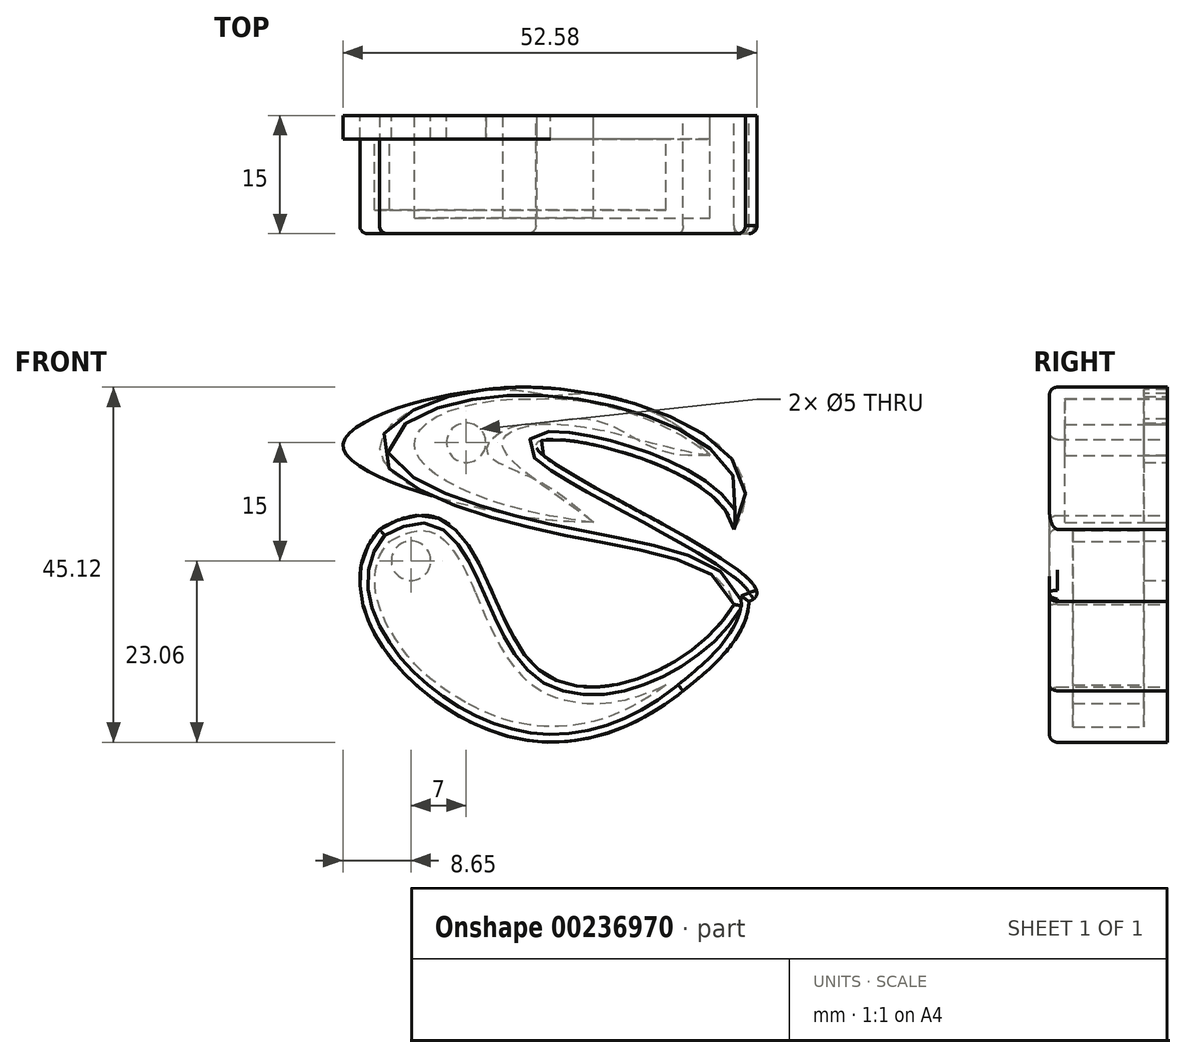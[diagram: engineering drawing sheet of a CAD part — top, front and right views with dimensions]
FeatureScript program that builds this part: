
annotation { "Feature Type Name" : "Feature", "Feature Type Description" : "" }
export const myFeature = defineFeature(function(context is Context, id is Id, definition is map)
    precondition{}
    {
        {
            var Q0;
            Q0=qCreatedBy(makeId("Front.planeOp"),FACE);
            var sketch = newSketch(context, id + "F0", { "sketchPlane" : qUnion([Q0])});
            skLineSegment(sketch, "E0", {"start": v(0, 18.03) * mm, "end": v(0, -26.97) * mm, "construction": true});
            skFitSpline(sketch, "E1", {"points": [v(25, 0) * mm, v(0, 18.03) * mm, v(-20, 10.22) * mm, v(0, 0) * mm, v(25, -9.54) * mm, v(0, -26.97) * mm, v(-20, 0) * mm], "startDerivative": vector(114.8, 173.45) * mm, "endDerivative": vector(137.84, 155.21) * mm});
            skLineSegment(sketch, "E2", {"start": v(-20, 0) * mm, "end": v(25, 0) * mm, "construction": true});
            skFitSpline(sketch, "E3", {"points": [v(25, 0) * mm, v(0, 10.22) * mm, v(25, -9.54) * mm], "startDerivative": vector(-9.3, 54.04) * mm, "endDerivative": vector(-76.27, -7.07) * mm});
            skFitSpline(sketch, "E4", {"points": [v(-20, 0) * mm, v(0, -17.65) * mm, v(25, -9.54) * mm], "startDerivative": vector(77.62, 45.8) * mm, "endDerivative": vector(25.53, 45.41) * mm});
            skFitSpline(sketch, "E5", {"points": [v(25.52, -5.18) * mm, v(17.95, -21.02) * mm], "startDerivative": vector(15.34, -20.4) * mm, "endDerivative": vector(-6.86, -5.89) * mm});
            skSolve(sketch);
        }
        {
            var Q0;
            Q0 = qSketchRegion(id + "F0", true);
            extrude(context, id + "F1", {"entities" : qUnion([Q0]), "depth" : 15 * mm});
        }
        {
            var Q0;
            Q0=makeQuery(id+"F1.opExtrude","CAP_FACE",FACE,{"disambiguationData":[OSD([sQuery(id+"F0.wireOp",EDGE,"E1"),sQuery(id+"F0.wireOp",EDGE,"E3"),sQuery(id+"F0.wireOp",EDGE,"E4"),sQuery(id+"F0.wireOp",EDGE,"E5"),sQuery(id+"F0.wireOp",EDGE,"E1")])],"isStart":true});
            var sketch = newSketch(context, id + "F2", { "sketchPlane" : qUnion([Q0])});
            skFitSpline(sketch, "E6.0", {"points": [v(-25, 0) * mm, v(-31.76, 10.22) * mm, v(1.18, 23.58) * mm, v(29, 9.83) * mm, v(0.24, -1.74) * mm, v(-37.75, -4.5) * mm, v(0.03, -41.05) * mm, v(28.48, -9.54) * mm, v(20, 0) * mm]});
            skFitSpline(sketch, "E7.0", {"points": [v(20, 0) * mm, v(7.02, 7.66) * mm, v(6.98, -30.5) * mm, v(-20.76, -17.08) * mm, v(-25, -9.54) * mm]});
            skFitSpline(sketch, "E8.0", {"points": [v(-25.52, -5.18) * mm, v(-30.63, -11.98) * mm, v(-20.23, -19.06) * mm, v(-17.95, -21.02) * mm]});
            skFitSpline(sketch, "E9.0", {"points": [v(-25, 0) * mm, v(-23.51, 8.63) * mm, v(30.37, 19.61) * mm, v(-38.24, -8.32) * mm, v(-25, -9.54) * mm]});
            skFitSpline(sketch, "E10.0", {"points": [v(-25, 0) * mm, v(-31.76, 10.22) * mm, v(1.18, 23.58) * mm, v(29, 9.83) * mm, v(0.24, -1.74) * mm, v(-37.75, -4.5) * mm, v(0.03, -41.05) * mm, v(28.48, -9.54) * mm, v(20, 0) * mm]});
            skFitSpline(sketch, "E11.0", {"points": [v(18.98, -1.72) * mm, v(18.25, -1.3) * mm, v(16.92, -0.64) * mm, v(15.34, -0.22) * mm, v(14.13, -0.2) * mm, v(13.16, -0.45) * mm, v(12.25, -0.98) * mm, v(11.33, -1.84) * mm, v(10.41, -3.03) * mm, v(9.24, -5) * mm, v(7.84, -8.02) * mm, v(6.43, -11.33) * mm, v(5.17, -13.93) * mm, v(4.11, -15.8) * mm, v(3.1, -17.26) * mm, v(2.18, -18.33) * mm, v(1.43, -19.08) * mm, v(0.6, -19.75) * mm, v(-0.55, -20.52) * mm, v(-2.09, -21.26) * mm, v(-4.04, -21.81) * mm, v(-6.72, -22.14) * mm, v(-10.14, -21.88) * mm, v(-14.2, -20.72) * mm, v(-18.07, -18.88) * mm, v(-21.59, -16.5) * mm, v(-24.6, -13.7) * mm, v(-26.13, -11.62) * mm, v(-26.74, -10.52) * mm]});
            skFitSpline(sketch, "E11.1", {"points": [v(-26.67, -1.1) * mm, v(-27.02, -0.58) * mm, v(-27.62, 0.49) * mm, v(-28.22, 2.11) * mm, v(-28.5, 3.75) * mm, v(-28.47, 5.37) * mm, v(-28.13, 6.92) * mm, v(-27.32, 8.86) * mm, v(-25.75, 11) * mm, v(-23.23, 13.17) * mm, v(-20.21, 15.03) * mm, v(-16.8, 16.6) * mm, v(-13.08, 17.89) * mm, v(-9.18, 18.9) * mm, v(-5.2, 19.6) * mm, v(-1.91, 19.95) * mm, v(0.65, 20.06) * mm, v(3.15, 20.06) * mm, v(6.13, 19.87) * mm, v(9.44, 19.38) * mm, v(12.46, 18.64) * mm, v(15.14, 17.69) * mm, v(17.46, 16.55) * mm, v(19.4, 15.22) * mm, v(20.66, 13.93) * mm, v(21.41, 12.74) * mm, v(21.82, 11.76) * mm, v(22.03, 10.7) * mm, v(21.99, 9.58) * mm, v(21.7, 8.54) * mm, v(21.23, 7.6) * mm, v(20.62, 6.76) * mm, v(19.66, 5.73) * mm, v(18.2, 4.58) * mm, v(16.13, 3.33) * mm, v(13.73, 2.18) * mm, v(11.05, 1.1) * mm, v(8.14, 0.1) * mm, v(5.04, -0.82) * mm, v(1.8, -1.65) * mm, v(-1.53, -2.4) * mm, v(-4.85, -3.05) * mm, v(-8.12, -3.68) * mm, v(-11.24, -4.3) * mm, v(-14.17, -4.94) * mm, v(-16.8, -5.63) * mm, v(-19.08, -6.4) * mm, v(-20.9, -7.27) * mm, v(-21.94, -8.02) * mm, v(-22.48, -8.6) * mm, v(-22.76, -9.01) * mm, v(-22.91, -9.35) * mm, v(-23, -9.64) * mm, v(-23.04, -9.94) * mm, v(-23.06, -10.4) * mm, v(-22.97, -11.06) * mm, v(-22.76, -11.83) * mm, v(-22.3, -12.97) * mm, v(-21.42, -14.54) * mm, v(-19.87, -16.53) * mm, v(-17.9, -18.5) * mm, v(-15.58, -20.37) * mm, v(-12.96, -22.03) * mm, v(-10.11, -23.42) * mm, v(-7.1, -24.44) * mm, v(-4.5, -24.93) * mm, v(-2.39, -25.07) * mm, v(-0.8, -25.05) * mm, v(0.79, -24.89) * mm, v(2.93, -24.48) * mm, v(5.63, -23.63) * mm, v(8.77, -22.14) * mm, v(12.72, -19.62) * mm, v(16.1, -16.45) * mm, v(18.55, -13.02) * mm, v(19.83, -10.4) * mm, v(20.51, -7.88) * mm, v(20.56, -5.52) * mm, v(19.97, -3.36) * mm, v(19.1, -2) * mm, v(18.5, -1.33) * mm]});
            skSolve(sketch);
        }
        {
            var Q0;
            {var subQ0=sQuery(id+"F2.wireOp",EDGE,"E11.0");Q0=makeQuery(id+"F2.imprint","IMPRINT",FACE,{"disambiguationData":[TD([[makeQuery(id+"F2.imprint","IMPRINT",EDGE,{"derivedFrom":subQ0}),1.0]])]});}
            var Q1;
            Q1=sQuery(id+"F2.wireOp",EDGE,"E11.1");
            var Q2;
            Q2=sQuery(id+"F2.wireOp",EDGE,"E11.0");
            extrude(context, id + "F3", {"entities" : qUnion([Q0]), "operationType" : NewBodyOperationType.REMOVE, "surfaceEntities" : qUnion([Q1, Q2]), "oppositeDirection" : true, "depth" : 12 * mm});
        }
        {
            var Q0;
            Q0=makeQuery(id+"F1.opExtrude","CAP_FACE",FACE,{"disambiguationData":[OSD([sQuery(id+"F0.wireOp",EDGE,"E1"),sQuery(id+"F0.wireOp",EDGE,"E3"),sQuery(id+"F0.wireOp",EDGE,"E4"),sQuery(id+"F0.wireOp",EDGE,"E5"),sQuery(id+"F0.wireOp",EDGE,"E1")])],"isStart":true});
            var sketch = newSketch(context, id + "F4", { "sketchPlane" : qUnion([Q0])});
            skFitSpline(sketch, "E12.0", {"points": [v(-26.67, -1.1) * mm, v(-27.02, -0.58) * mm, v(-27.62, 0.49) * mm, v(-28.22, 2.11) * mm, v(-28.5, 3.75) * mm, v(-28.47, 5.37) * mm, v(-28.13, 6.92) * mm, v(-27.32, 8.86) * mm, v(-25.75, 11) * mm, v(-23.23, 13.17) * mm, v(-20.21, 15.03) * mm, v(-16.8, 16.6) * mm, v(-13.08, 17.89) * mm, v(-9.18, 18.9) * mm, v(-5.2, 19.6) * mm, v(-1.91, 19.95) * mm, v(0.65, 20.06) * mm, v(3.15, 20.06) * mm, v(6.13, 19.87) * mm, v(9.44, 19.38) * mm, v(12.46, 18.64) * mm, v(15.14, 17.69) * mm, v(17.46, 16.55) * mm, v(19.4, 15.22) * mm, v(20.66, 13.93) * mm, v(21.41, 12.74) * mm, v(21.82, 11.76) * mm, v(22.03, 10.7) * mm, v(21.99, 9.58) * mm, v(21.7, 8.54) * mm, v(21.23, 7.6) * mm, v(20.62, 6.76) * mm, v(19.66, 5.73) * mm, v(18.2, 4.58) * mm, v(16.13, 3.33) * mm, v(13.73, 2.18) * mm, v(11.05, 1.1) * mm, v(8.14, 0.1) * mm, v(5.04, -0.82) * mm, v(1.8, -1.65) * mm, v(-1.53, -2.4) * mm, v(-4.85, -3.05) * mm, v(-8.12, -3.68) * mm, v(-11.24, -4.3) * mm, v(-14.17, -4.94) * mm, v(-16.8, -5.63) * mm, v(-19.08, -6.4) * mm, v(-20.9, -7.27) * mm, v(-21.94, -8.02) * mm, v(-22.48, -8.6) * mm, v(-22.76, -9.01) * mm, v(-22.91, -9.35) * mm, v(-23, -9.64) * mm, v(-23.04, -9.94) * mm, v(-23.06, -10.4) * mm, v(-22.97, -11.06) * mm, v(-22.76, -11.83) * mm, v(-22.3, -12.97) * mm, v(-21.42, -14.54) * mm, v(-19.87, -16.53) * mm, v(-17.9, -18.5) * mm, v(-15.58, -20.37) * mm, v(-12.96, -22.03) * mm, v(-10.11, -23.42) * mm, v(-7.1, -24.44) * mm, v(-4.5, -24.93) * mm, v(-2.39, -25.07) * mm, v(-0.8, -25.05) * mm, v(0.79, -24.89) * mm, v(2.93, -24.48) * mm, v(5.63, -23.63) * mm, v(8.77, -22.14) * mm, v(12.72, -19.62) * mm, v(16.1, -16.45) * mm, v(18.55, -13.02) * mm, v(19.83, -10.4) * mm, v(20.51, -7.88) * mm, v(20.56, -5.52) * mm, v(19.97, -3.36) * mm, v(19.1, -2) * mm, v(18.5, -1.33) * mm]});
            skFitSpline(sketch, "E13.0", {"points": [v(18.98, -1.72) * mm, v(18.25, -1.3) * mm, v(16.92, -0.64) * mm, v(15.34, -0.22) * mm, v(14.13, -0.2) * mm, v(13.16, -0.45) * mm, v(12.25, -0.98) * mm, v(11.33, -1.84) * mm, v(10.41, -3.03) * mm, v(9.24, -5) * mm, v(7.84, -8.02) * mm, v(6.43, -11.33) * mm, v(5.17, -13.93) * mm, v(4.11, -15.8) * mm, v(3.1, -17.26) * mm, v(2.18, -18.33) * mm, v(1.43, -19.08) * mm, v(0.6, -19.75) * mm, v(-0.55, -20.52) * mm, v(-2.09, -21.26) * mm, v(-4.04, -21.81) * mm, v(-6.72, -22.14) * mm, v(-10.14, -21.88) * mm, v(-14.2, -20.72) * mm, v(-18.07, -18.88) * mm, v(-21.59, -16.5) * mm, v(-24.6, -13.7) * mm, v(-26.13, -11.62) * mm, v(-26.74, -10.52) * mm]});
            skSolve(sketch);
        }
        {
            var Q0;
            Q0 = qSketchRegion(id + "F4", true);
            var Q1;
            Q1=makeQuery(id+"F4.imprint","IMPRINT",FACE,{"disambiguationData":[TD([[makeQuery(id+"F4.imprint","IMPRINT",EDGE,{"derivedFrom":sQuery(id+"F4.wireOp",EDGE,"E12.0")}),-1.0]])]});
            extrude(context, id + "F5", {"entities" : qUnion([Q0, Q1]), "operationType" : NewBodyOperationType.ADD, "oppositeDirection" : true, "depth" : 3 * mm});
        }
        {
            var Q0;
            {var subQ0=sQuery(id+"F0.wireOp",EDGE,"E1");var subQ1=sQuery(id+"F0.wireOp",EDGE,"E5");var subQ2=sQuery(id+"F0.wireOp",EDGE,"E4");var subQ3=sQuery(id+"F0.wireOp",EDGE,"E3");var subQ4=sQuery(id+"F0.wireOp",EDGE,"E1");Q0=makeQuery(id+"F5.boolean.opBoolean","MERGE",FACE,{"derivedFrom":[makeQuery(id+"F1.opExtrude","CAP_FACE",FACE,{"disambiguationData":[OSD([subQ4,subQ3,subQ2,subQ1,subQ0])],"isStart":true}),makeQuery(id+"F5.opExtrude","CAP_FACE",FACE,{"disambiguationData":[OSD([subQ4,subQ3,subQ2,subQ1,subQ0])],"isStart":true})]});}
            var sketch = newSketch(context, id + "F6", { "sketchPlane" : qUnion([Q0])});
            skCircle(sketch, "E14", {"center": v(16, -4) * mm, "radius": 2.5 * mm});
            skSolve(sketch);
        }
        {
            var Q0;
            Q0 = qSketchRegion(id + "F6", true);
            extrude(context, id + "F7", {"entities" : qUnion([Q0]), "operationType" : NewBodyOperationType.REMOVE, "endBound" : BoundingType.UP_TO_NEXT, "oppositeDirection" : true, "depth" : 25 * mm});
        }
        {
            var Q0;
            {var subQ0=sQuery(id+"F0.wireOp",EDGE,"E1");var subQ1=sQuery(id+"F0.wireOp",EDGE,"E5");var subQ2=sQuery(id+"F0.wireOp",EDGE,"E4");var subQ3=sQuery(id+"F0.wireOp",EDGE,"E3");var subQ4=sQuery(id+"F0.wireOp",EDGE,"E1");Q0=makeQuery(id+"F5.boolean.opBoolean","MERGE",FACE,{"derivedFrom":[makeQuery(id+"F1.opExtrude","CAP_FACE",FACE,{"disambiguationData":[OSD([subQ4,subQ3,subQ2,subQ1,subQ0])],"isStart":true}),makeQuery(id+"F5.opExtrude","CAP_FACE",FACE,{"disambiguationData":[OSD([subQ4,subQ3,subQ2,subQ1,subQ0])],"isStart":true})]});}
            var sketch = newSketch(context, id + "F8", { "sketchPlane" : qUnion([Q0])});
            skFitSpline(sketch, "E15", {"points": [v(-7.15, 0.9) * mm, v(15.58, 10.64) * mm, v(-3.75, 16.3) * mm], "startDerivative": vector(69.57, 7.17) * mm, "endDerivative": vector(-73.1, -8.1) * mm});
            skFitSpline(sketch, "E16", {"points": [v(-7.15, 0.9) * mm, v(4.38, 10.64) * mm, v(0, 13.28) * mm], "startDerivative": vector(33.96, 25.28) * mm, "endDerivative": vector(-28.33, 3.56) * mm});
            skFitSpline(sketch, "E17", {"points": [v(0, 16.57) * mm, v(-21.98, 9.35) * mm], "startDerivative": vector(-23.2, 1.6) * mm, "endDerivative": vector(-13.31, -12) * mm});
            skFitSpline(sketch, "E18", {"points": [v(-21.98, 9.35) * mm, v(0, 13.28) * mm], "startDerivative": vector(20.3, 2.4) * mm, "endDerivative": vector(23.4, -1.3) * mm});
            skSolve(sketch);
        }
        {
            var Q0;
            Q0 = qSketchRegion(id + "F8", true);
            extrude(context, id + "F9", {"entities" : qUnion([Q0]), "operationType" : NewBodyOperationType.REMOVE, "oppositeDirection" : true, "depth" : 13 * mm});
        }
        {
            var Q0;
            {var subQ0=sQuery(id+"F0.wireOp",EDGE,"E1");var subQ1=sQuery(id+"F0.wireOp",EDGE,"E5");var subQ2=sQuery(id+"F0.wireOp",EDGE,"E4");var subQ3=sQuery(id+"F0.wireOp",EDGE,"E3");var subQ4=sQuery(id+"F0.wireOp",EDGE,"E1");Q0=makeQuery(id+"F5.boolean.opBoolean","MERGE",FACE,{"derivedFrom":[makeQuery(id+"F1.opExtrude","CAP_FACE",FACE,{"disambiguationData":[OSD([subQ4,subQ3,subQ2,subQ1,subQ0])],"isStart":true}),makeQuery(id+"F5.opExtrude","CAP_FACE",FACE,{"disambiguationData":[OSD([subQ4,subQ3,subQ2,subQ1,subQ0])],"isStart":true})]});}
            var sketch = newSketch(context, id + "F10", { "sketchPlane" : qUnion([Q0])});
            skFitSpline(sketch, "E19.0.0", {"points": [v(0, 16.57) * mm, v(-7.73, 17.1) * mm, v(-17.55, 13.35) * mm, v(-21.98, 9.35) * mm]});
            skFitSpline(sketch, "E19.0.1", {"points": [v(-21.98, 9.35) * mm, v(-15.22, 10.15) * mm, v(-7.8, 13.72) * mm, v(0, 13.28) * mm]});
            skFitSpline(sketch, "E19.0.2", {"points": [v(0, 13.28) * mm, v(3.47, 12.84) * mm, v(6.44, 10.03) * mm, v(0, 6.22) * mm, v(-7.15, 0.9) * mm]});
            skFitSpline(sketch, "E19.0.3", {"points": [v(-7.15, 0.9) * mm, v(5.04, 2.15) * mm, v(24.65, 10.62) * mm, v(7.81, 17.59) * mm, v(-3.75, 16.3) * mm]});
            skSolve(sketch);
        }
        {
            var Q0;
            Q0 = qSketchRegion(id + "F10", true);
            extrude(context, id + "F11", {"entities" : qUnion([Q0]), "oppositeDirection" : true, "depth" : 3 * mm});
        }
        {
            var Q0;
            Q0=makeQuery(id+"F11.opExtrude","CAP_FACE",FACE,{"disambiguationData":[OSD([sQuery(id+"F10.wireOp",EDGE,"E19.0.0"),sQuery(id+"F10.wireOp",EDGE,"E19.0.1"),sQuery(id+"F10.wireOp",EDGE,"E19.0.2"),sQuery(id+"F10.wireOp",EDGE,"E19.0.3")])],"isStart":true});
            var sketch = newSketch(context, id + "F12", { "sketchPlane" : qUnion([Q0])});
            skCircle(sketch, "E20", {"center": v(9, 11) * mm, "radius": 2.5 * mm});
            skSolve(sketch);
        }
        {
            var Q0;
            Q0 = qSketchRegion(id + "F12", true);
            extrude(context, id + "F13", {"entities" : qUnion([Q0]), "operationType" : NewBodyOperationType.REMOVE, "oppositeDirection" : true, "depth" : 5 * mm});
        }
        {
            var Q0;
            Q0=makeQuery(id+"F1.opExtrude","CAP_EDGE",EDGE,{"disambiguationData":[OSD([sQuery(id+"F0.wireOp",EDGE,"E5")])],"isStart":false});
            var Q1;
            Q1=makeQuery(id+"F1.opExtrude","CAP_EDGE",EDGE,{"disambiguationData":[OSD([sQuery(id+"F0.wireOp",EDGE,"E1")])],"isStart":false});
            var Q2;
            Q2=makeQuery(id+"F1.opExtrude","CAP_EDGE",EDGE,{"disambiguationData":[OSD([sQuery(id+"F0.wireOp",EDGE,"E4")])],"isStart":false});
            var Q3;
            Q3=makeQuery(id+"F1.opExtrude","CAP_EDGE",EDGE,{"disambiguationData":[OSD([sQuery(id+"F0.wireOp",EDGE,"E1")])],"isStart":false});
            var Q4;
            Q4=makeQuery(id+"F1.opExtrude","CAP_EDGE",EDGE,{"disambiguationData":[OSD([sQuery(id+"F0.wireOp",EDGE,"E3")])],"isStart":false});
            fillet(context, id + "F14", {"entities" : qUnion([Q0, Q1, Q2, Q3, Q4]), "radius" : 1 * mm, "tangentPropagation" : true, "allowEdgeOverflow" : false});
        }
    });
